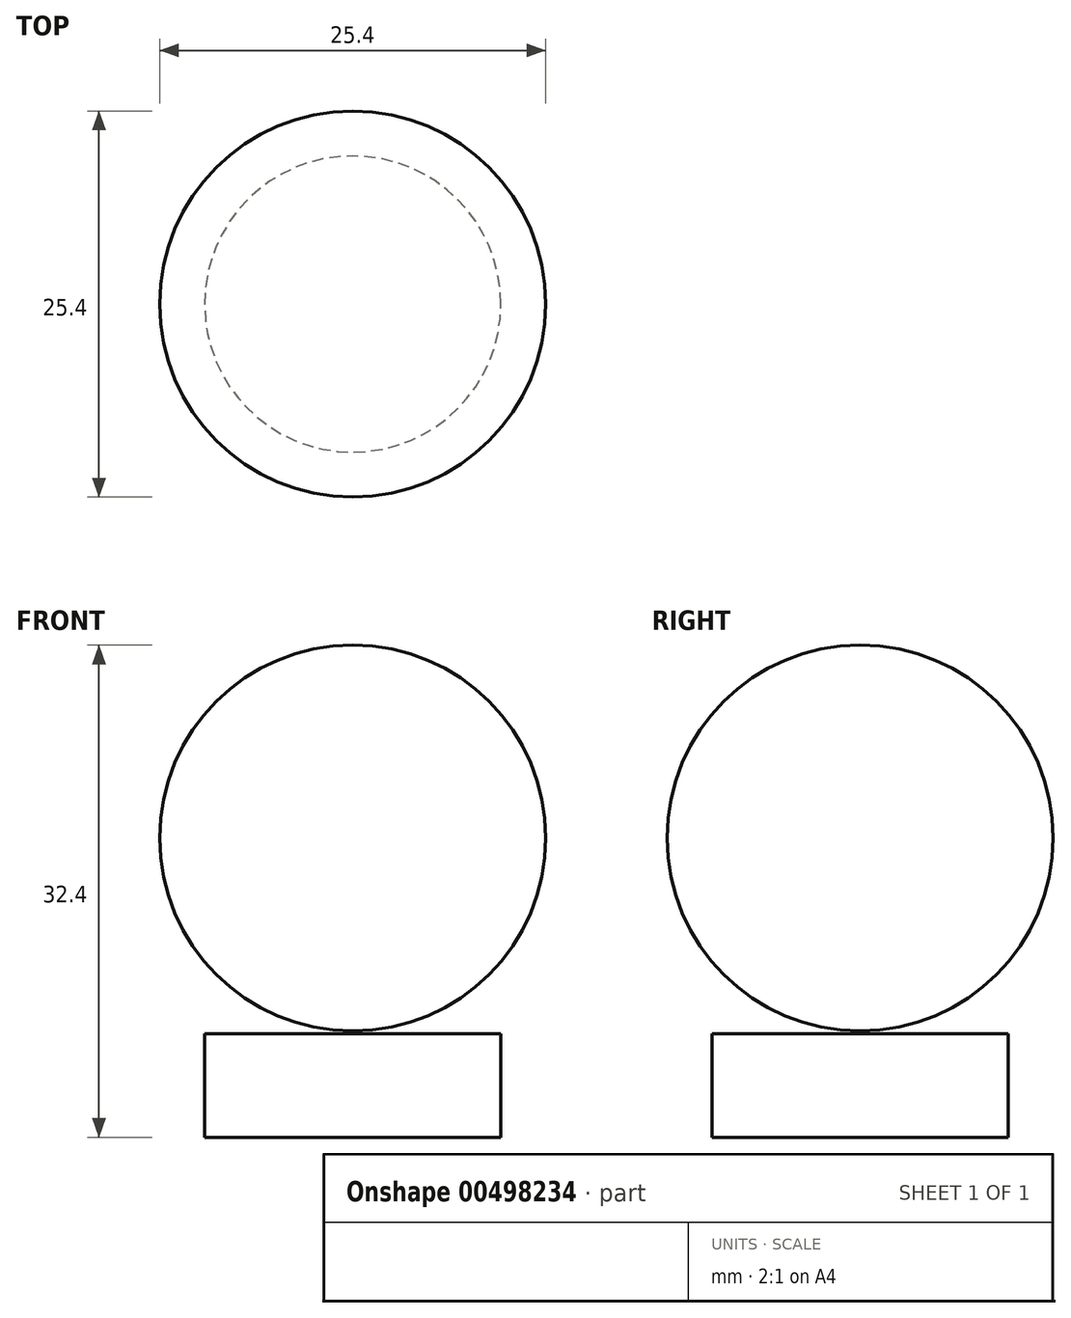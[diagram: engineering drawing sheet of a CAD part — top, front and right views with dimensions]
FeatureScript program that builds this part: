
annotation { "Feature Type Name" : "Feature", "Feature Type Description" : "" }
export const myFeature = defineFeature(function(context is Context, id is Id, definition is map)
    precondition{}
    {
        {
            var Q0;
            Q0=qCreatedBy(makeId("Front.planeOp"),FACE);
            var sketch = newSketch(context, id + "F0", { "sketchPlane" : qUnion([Q0])});
            skArc(sketch, "E0", {"start": v(0, 7) * mm, "mid": v(12.7, 19.7) * mm, "end": v(0, 32.4) * mm});
            skLineSegment(sketch, "E1", {"start": v(0, 32.4) * mm, "end": v(0, 7) * mm});
            skSolve(sketch);
        }
        {
            var Q0;
            Q0 = qSketchRegion(id + "F0", true);
            var Q1;
            Q1=sQuery(id+"F0.wireOp",EDGE,"E1");
            revolve(context, id + "F1", {"entities" : qUnion([Q0]), "axis" : qUnion([Q1]), "revolveType" : RevolveType.FULL});
        }
        {
            var Q0;
            Q0=qCreatedBy(makeId("Front.planeOp"),FACE);
            var sketch = newSketch(context, id + "F2", { "sketchPlane" : qUnion([Q0])});
            skCircle(sketch, "E2", {"center": v(0, 19.7) * mm, "radius": 12.7 * mm});
            skLineSegment(sketch, "E3", {"start": v(-8.98, 10.72) * mm, "end": v(-18.86, 20.6) * mm, "construction": true});
            skLineSegment(sketch, "E4", {"start": v(-8.98, 10.72) * mm, "end": v(-20.26, 10.72) * mm, "construction": true});
            skSolve(sketch);
        }
        {
            var Q0;
            Q0=qCreatedBy(makeId("Top.planeOp"),FACE);
            var sketch = newSketch(context, id + "F3", { "sketchPlane" : qUnion([Q0])});
            skCircle(sketch, "E5", {"center": v(0, 0) * mm, "radius": 9.75 * mm});
            skSolve(sketch);
        }
        {
            var Q0;
            Q0 = qSketchRegion(id + "F3", true);
            var Q1;
            Q1=makeQuery(id+"F1.opRevolve","SWEPT_BODY",BODY,{"disambiguationData":[OSD([sQuery(id+"F0.wireOp",EDGE,"E0"),sQuery(id+"F0.wireOp",EDGE,"E1")])]});
            extrude(context, id + "F4", {"entities" : qUnion([Q0]), "endBoundEntityBody" : qUnion([Q1]), "depth" : 6.8 * mm});
        }
        {
            var Q0;
            Q0=qCreatedBy(makeId("Front.planeOp"),FACE);
            var sketch = newSketch(context, id + "F5", { "sketchPlane" : qUnion([Q0])});
            skArc(sketch, "E6.0", {"start": v(0, 6.8) * mm, "mid": v(5.3, 7.94) * mm, "end": v(9.67, 11.17) * mm});
            skLineSegment(sketch, "E7", {"start": v(9.67, 11.17) * mm, "end": v(9.67, 6.8) * mm});
            skLineSegment(sketch, "E8", {"start": v(9.67, 6.8) * mm, "end": v(0, 6.8) * mm});
            skLineSegment(sketch, "E9", {"start": v(0, 6.8) * mm, "end": v(0, 6.97) * mm, "construction": true});
            skSolve(sketch);
        }
        {
            var Q0;
            Q0=makeQuery(id+"F5.imprint","IMPRINT",FACE,{"disambiguationData":[TD([[makeQuery(id+"F5.imprint","IMPRINT",EDGE,{"derivedFrom":sQuery(id+"F5.wireOp",EDGE,"E6.0")}),-1.0]])]});
            var Q1;
            Q1=sQuery(id+"F5.wireOp",EDGE,"E7");
            var Q2;
            Q2=sQuery(id+"F5.wireOp",EDGE,"E6.0");
            var Q3;
            Q3=sQuery(id+"F5.wireOp",EDGE,"E9");
            revolve(context, id + "F6", {"bodyType" : ToolBodyType.SURFACE, "operationType" : NewBodyOperationType.ADD, "entities" : qUnion([Q0]), "surfaceEntities" : qUnion([Q1, Q2]), "axis" : qUnion([Q3]), "revolveType" : RevolveType.FULL});
        }
    });
